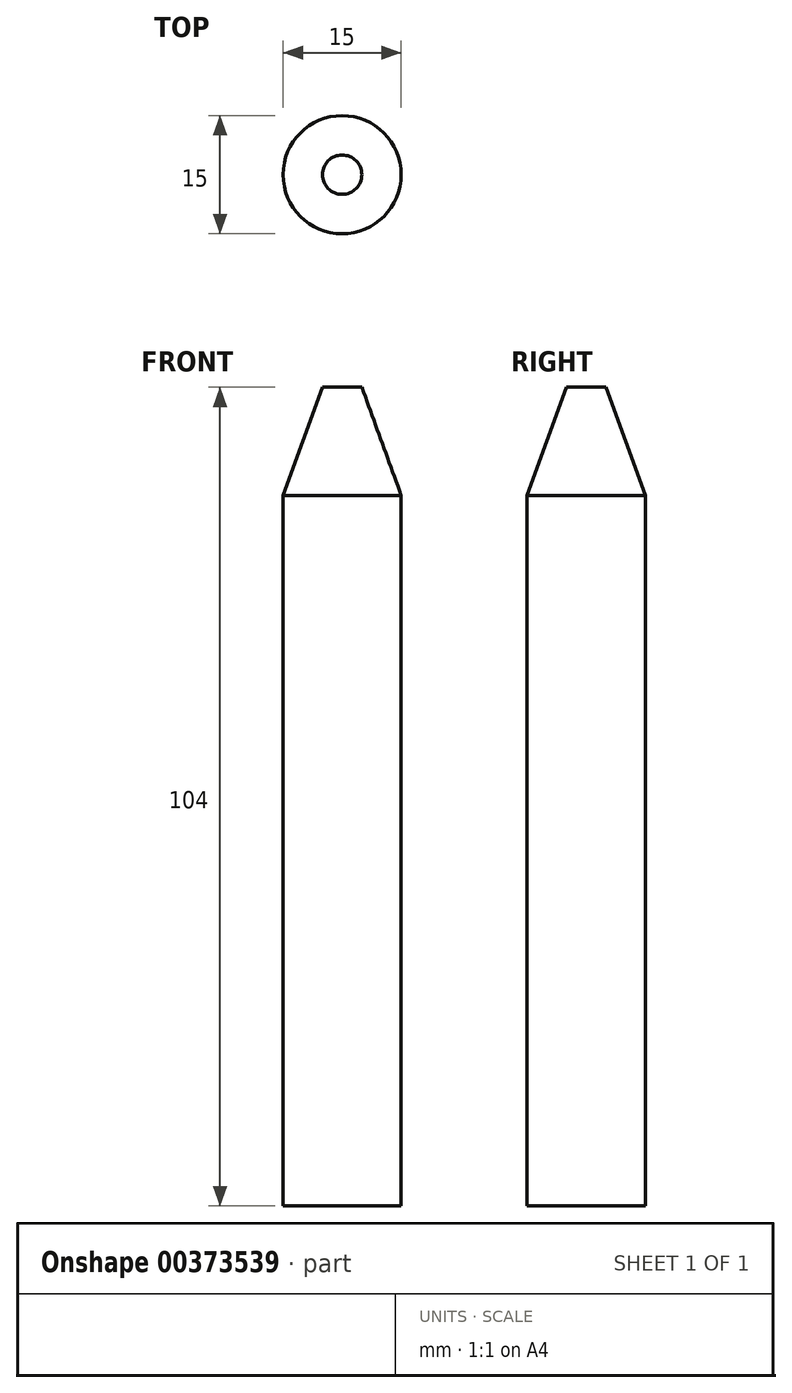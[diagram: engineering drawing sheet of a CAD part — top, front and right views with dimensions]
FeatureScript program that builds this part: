
annotation { "Feature Type Name" : "Feature", "Feature Type Description" : "" }
export const myFeature = defineFeature(function(context is Context, id is Id, definition is map)
    precondition{}
    {
        {
            var Q0;
            Q0=qCreatedBy(makeId("Top.planeOp"),FACE);
            var sketch = newSketch(context, id + "F0", { "sketchPlane" : qUnion([Q0])});
            skCircle(sketch, "E0", {"center": v(0, 12.99) * mm, "radius": 7.5 * mm});
            skSolve(sketch);
        }
        {
            var Q0;
            Q0=makeQuery(id+"F0.imprint","IMPRINT",FACE,{"disambiguationData":[TD([[makeQuery(id+"F0.imprint","IMPRINT",EDGE,{"derivedFrom":sQuery(id+"F0.wireOp",EDGE,"E0")}),1.0]])]});
            extrude(context, id + "F1", {"entities" : qUnion([Q0]), "depth" : 104 * mm});
        }
        {
            var Q0;
            Q0=makeQuery(id+"F1.opExtrude","CAP_EDGE",EDGE,{"disambiguationData":[OSD([sQuery(id+"F0.wireOp",EDGE,"E0")])],"isStart":false});
            chamfer(context, id + "F2", {"entities" : qUnion([Q0]), "chamferType" : ChamferType.OFFSET_ANGLE, "width" : 5 * mm, "oppositeDirection" : false, "angle" : 70 * degree, "tangentPropagation" : true});
        }
    });
